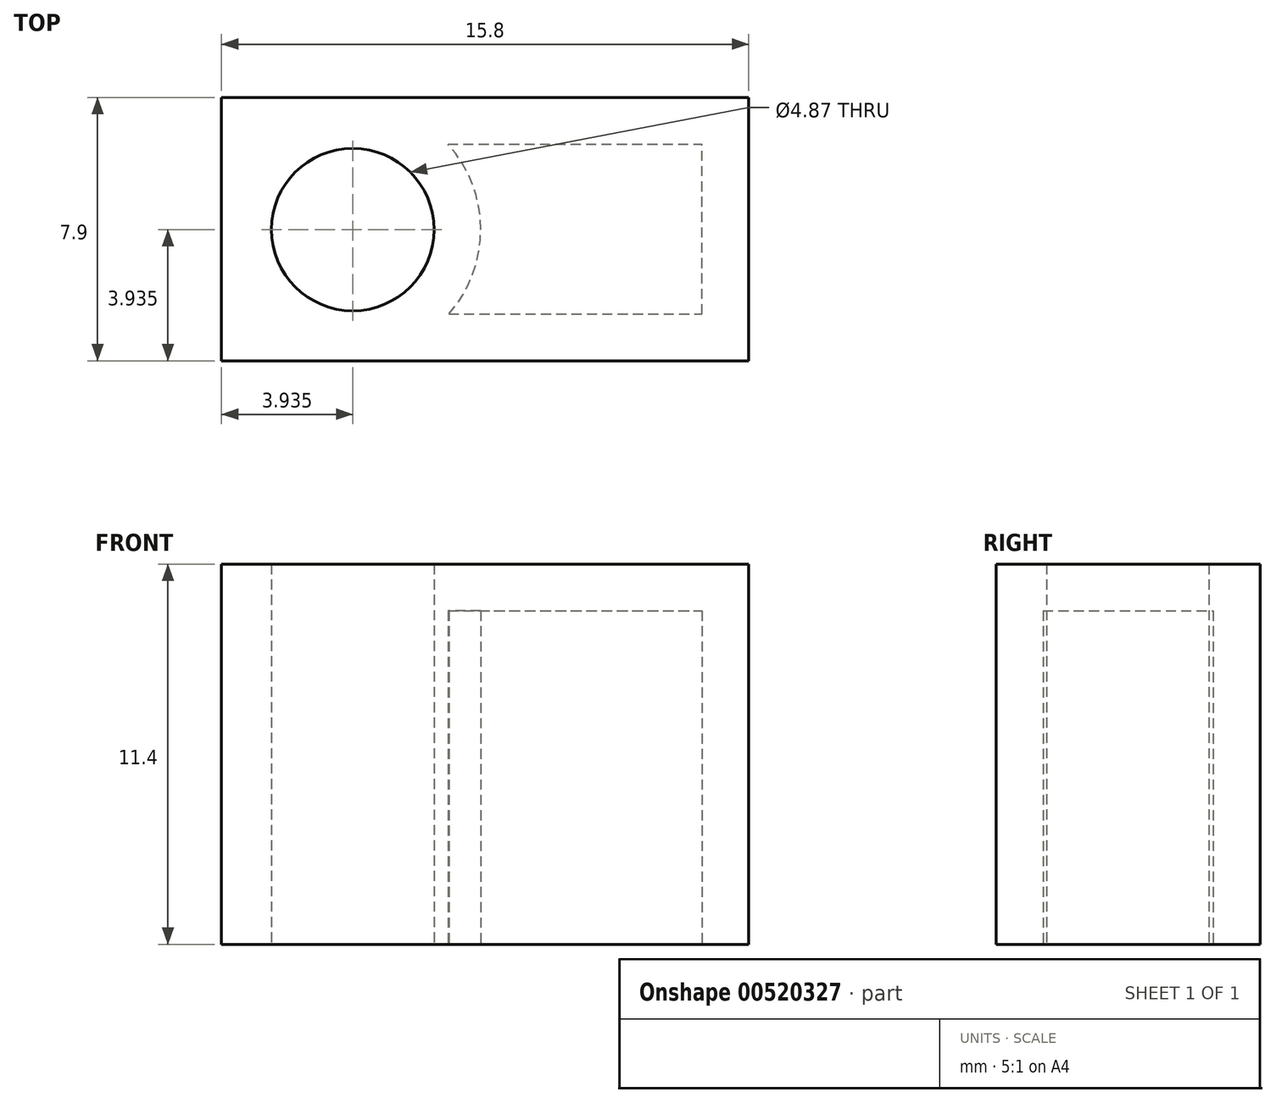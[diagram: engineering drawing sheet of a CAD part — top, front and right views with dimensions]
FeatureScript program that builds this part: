
annotation { "Feature Type Name" : "Feature", "Feature Type Description" : "" }
export const myFeature = defineFeature(function(context is Context, id is Id, definition is map)
    precondition{}
    {
        {
            var Q0;
            Q0=qCreatedBy(makeId("Top.planeOp"),FACE);
            var sketch = newSketch(context, id + "F0", { "sketchPlane" : qUnion([Q0])});
            skLineSegment(sketch, "E0.top", {"start": v(-7.9, -7.9) * mm, "end": v(7.9, -7.9) * mm});
            skPoint(sketch, "E0.middle", {"position": v(0, 0) * mm});
            skPoint(sketch, "E1.endSnap0", {"position": v(0, 7.9) * mm});
            skCircle(sketch, "E2.MirrorC", {"center": v(-3.96, -3.97) * mm, "radius": 2.44 * mm});
            skCircle(sketch, "E3.MirrorC", {"center": v(3.96, -3.97) * mm, "radius": 2.44 * mm});
            skLineSegment(sketch, "E4", {"start": v(-7.9, 0) * mm, "end": v(7.9, 0) * mm});
            skLineSegment(sketch, "E5", {"start": v(7.9, -7.9) * mm, "end": v(7.9, 0) * mm});
            skLineSegment(sketch, "E6", {"start": v(-7.9, -7.9) * mm, "end": v(-7.9, 0) * mm});
            skSolve(sketch);
        }
        {
            var Q0;
            Q0=makeQuery(id+"F0.imprint","IMPRINT",FACE,{"disambiguationData":[TD([[makeQuery(id+"F0.imprint","IMPRINT",EDGE,{"derivedFrom":sQuery(id+"F0.wireOp",EDGE,"E0.top")}),1.0]])]});
            extrude(context, id + "F1", {"entities" : qUnion([Q0]), "depth" : 9.6 * mm, "offsetDistance" : 25 * mm});
        }
        {
            var Q0;
            Q0=makeQuery(id+"F0.imprint","IMPRINT",FACE,{"disambiguationData":[TD([[makeQuery(id+"F0.imprint","IMPRINT",EDGE,{"derivedFrom":sQuery(id+"F0.wireOp",EDGE,"P5Uv2Dyq-tAQW-01s9-hLAb-62AKAhi8vcOe")}),1.0]])]});
            var Q1;
            Q1=makeQuery(id+"F0.imprint","IMPRINT",FACE,{"disambiguationData":[TD([[makeQuery(id+"F0.imprint","IMPRINT",EDGE,{"derivedFrom":sQuery(id+"F0.wireOp",EDGE,"92e43016-8348-4ffb-b2e2-6b4740cb38940.MirrorC")}),-1.0]])]});
            var Q2;
            Q2=makeQuery(id+"F0.imprint","IMPRINT",FACE,{"disambiguationData":[TD([[makeQuery(id+"F0.imprint","IMPRINT",EDGE,{"derivedFrom":sQuery(id+"F0.wireOp",EDGE,"E3.MirrorC")}),1.0]])]});
            var Q3;
            Q3=makeQuery(id+"F0.imprint","IMPRINT",FACE,{"disambiguationData":[TD([[makeQuery(id+"F0.imprint","IMPRINT",EDGE,{"derivedFrom":sQuery(id+"F0.wireOp",EDGE,"E2.MirrorC")}),-1.0]])]});
            extrude(context, id + "F2", {"entities" : qUnion([Q0, Q1, Q2, Q3]), "operationType" : NewBodyOperationType.ADD, "depth" : 11.4 * mm, "offsetDistance" : 25 * mm});
        }
        {
            var Q0;
            {var subQ0=sQuery(id+"F0.wireOp",EDGE,"E3.MirrorC");var subQ1=sQuery(id+"F0.wireOp",EDGE,"E2.MirrorC");Q0=makeQuery(id+"F2.boolean.opBoolean","MERGE",FACE,{"derivedFrom":[makeQuery(id+"F1.opExtrude","CAP_FACE",FACE,{"disambiguationData":[OSD([sQuery(id+"F0.wireOp",EDGE,"E0.top"),subQ1,subQ0,sQuery(id+"F0.wireOp",EDGE,"E4"),sQuery(id+"F0.wireOp",EDGE,"E5"),sQuery(id+"F0.wireOp",EDGE,"E6")])],"isStart":true}),makeQuery(id+"F2.opExtrude","CAP_FACE",FACE,{"disambiguationData":[OSD([subQ1])],"isStart":true}),makeQuery(id+"F2.opExtrude","CAP_FACE",FACE,{"disambiguationData":[OSD([subQ0])],"isStart":true})]});}
            shell(context, id + "F3", {"entities" : qUnion([Q0]), "thickness" : 1.4 * mm});
        }
    });
